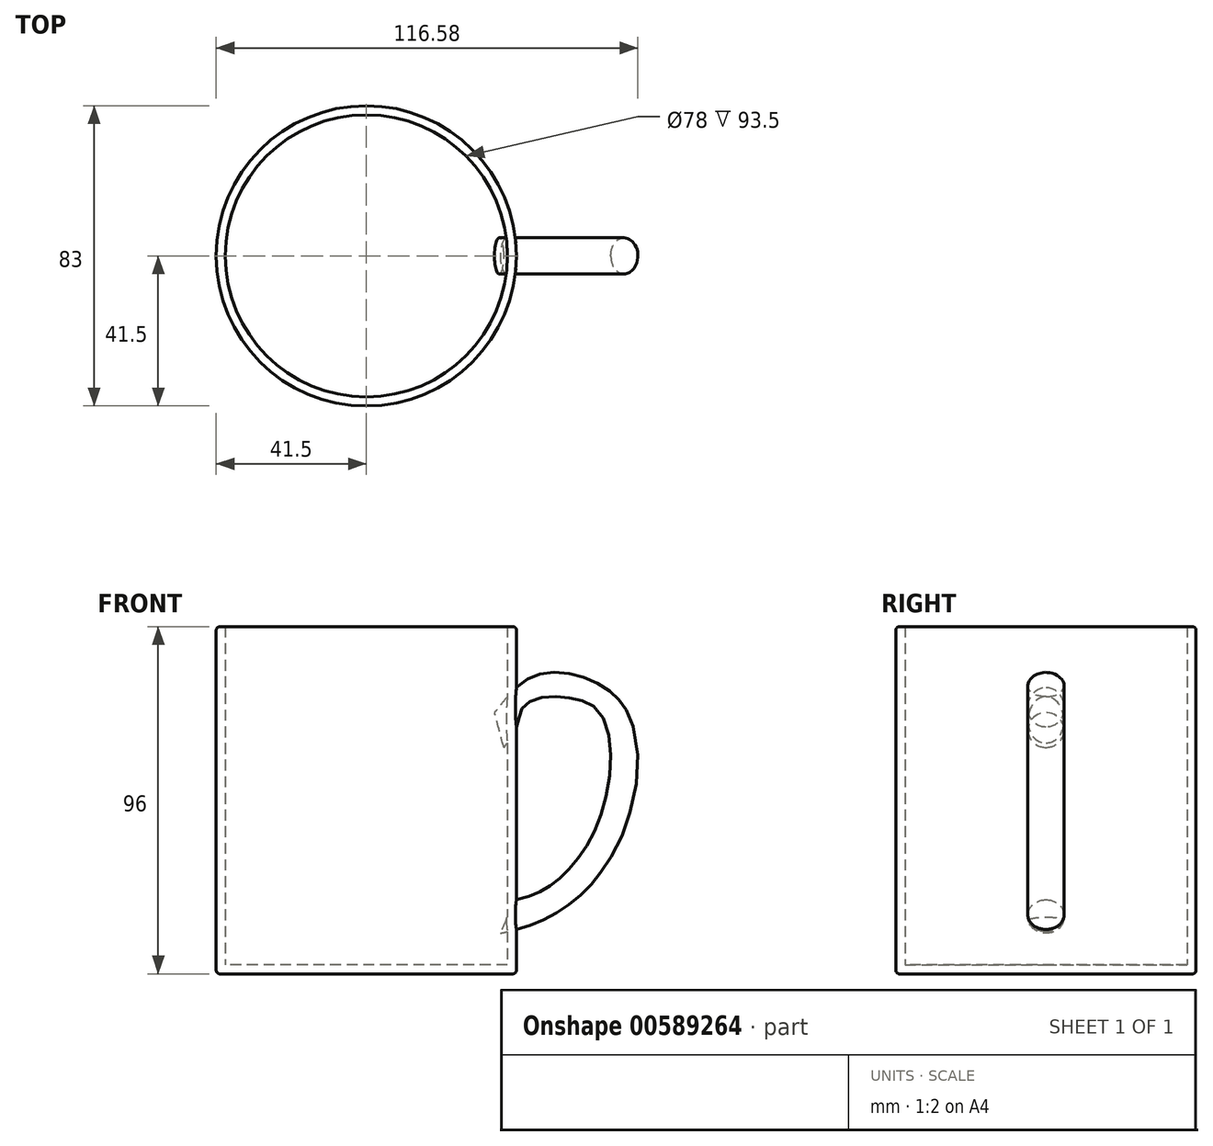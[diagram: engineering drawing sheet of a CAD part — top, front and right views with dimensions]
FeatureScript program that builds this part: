
annotation { "Feature Type Name" : "Feature", "Feature Type Description" : "" }
export const myFeature = defineFeature(function(context is Context, id is Id, definition is map)
    precondition{}
    {
        {
            var Q0;
            Q0=qCreatedBy(makeId("Top.planeOp"),FACE);
            var sketch = newSketch(context, id + "F0", { "sketchPlane" : qUnion([Q0])});
            skCircle(sketch, "E0", {"center": v(0, 0) * mm, "radius": 41.5 * mm});
            skSolve(sketch);
        }
        {
            var Q0;
            Q0=makeQuery(id+"F0.imprint","IMPRINT",FACE,{"disambiguationData":[TD([[makeQuery(id+"F0.imprint","IMPRINT",EDGE,{"derivedFrom":sQuery(id+"F0.wireOp",EDGE,"E0")}),1.0]])]});
            extrude(context, id + "F1", {"entities" : qUnion([Q0]), "depth" : 96 * mm, "offsetDistance" : 25 * mm});
        }
        {
            var Q0;
            Q0=makeQuery(id+"F1.opExtrude","CAP_FACE",FACE,{"disambiguationData":[OSD([sQuery(id+"F0.wireOp",EDGE,"E0")])],"isStart":false});
            shell(context, id + "F2", {"entities" : qUnion([Q0]), "thickness" : 2.5 * mm});
        }
        {
            var Q0;
            Q0=qCreatedBy(makeId("Front.planeOp"),FACE);
            var sketch = newSketch(context, id + "F3", { "sketchPlane" : qUnion([Q0])});
            skFitSpline(sketch, "E1", {"points": [v(34.82, 74.46) * mm, v(48.1, 84.74) * mm, v(72.96, 74.67) * mm, v(71.03, 34.6) * mm, v(51.32, 14.04) * mm, v(36.1, 9.1) * mm], "startDerivative": vector(65.67, 81.88) * mm, "endDerivative": vector(-93.02, -20.52) * mm});
            skSolve(sketch);
        }
        {
            var Q0;
            Q0=qCreatedBy(makeId("Right.planeOp"),FACE);
            cPlane(context, id + "F4", {"entities" : qUnion([Q0]), "cplaneType" : CPlaneType.OFFSET, "offset" : 42 * mm, "width" : 150 * mm, "height" : 150 * mm});
        }
        {
            var Q0;
            Q0=qCreatedBy(id+"F4.planeOp",FACE);
            var sketch = newSketch(context, id + "F5", { "sketchPlane" : qUnion([Q0])});
            skCircle(sketch, "E2", {"center": v(0, 74.67) * mm, "radius": 5 * mm});
            skSolve(sketch);
        }
        {
            var Q0;
            Q0=makeQuery(id+"F5.imprint","IMPRINT",FACE,{"disambiguationData":[TD([[makeQuery(id+"F5.imprint","IMPRINT",EDGE,{"derivedFrom":sQuery(id+"F5.wireOp",EDGE,"E2")}),1.0]])]});
            var Q1;
            Q1=sQuery(id+"F3.wireOp",EDGE,"E1");
            sweep(context, id + "F6", {"operationType" : NewBodyOperationType.ADD, "profiles" : qUnion([Q0]), "path" : qUnion([Q1])});
        }
        {
            var Q0;
            Q0=makeQuery(id+"F1.opExtrude","CAP_EDGE",EDGE,{"disambiguationData":[OSD([sQuery(id+"F0.wireOp",EDGE,"E0")])],"isStart":false});
            var Q1;
            Q1=makeQuery(id+"F1.opExtrude","CAP_EDGE",EDGE,{"disambiguationData":[OSD([sQuery(id+"F0.wireOp",EDGE,"E0")])],"isStart":true});
            fillet(context, id + "F7", {"entities" : qUnion([Q0, Q1]), "radius" : 1 * mm, "tangentPropagation" : true, "allowEdgeOverflow" : false});
        }
    });
